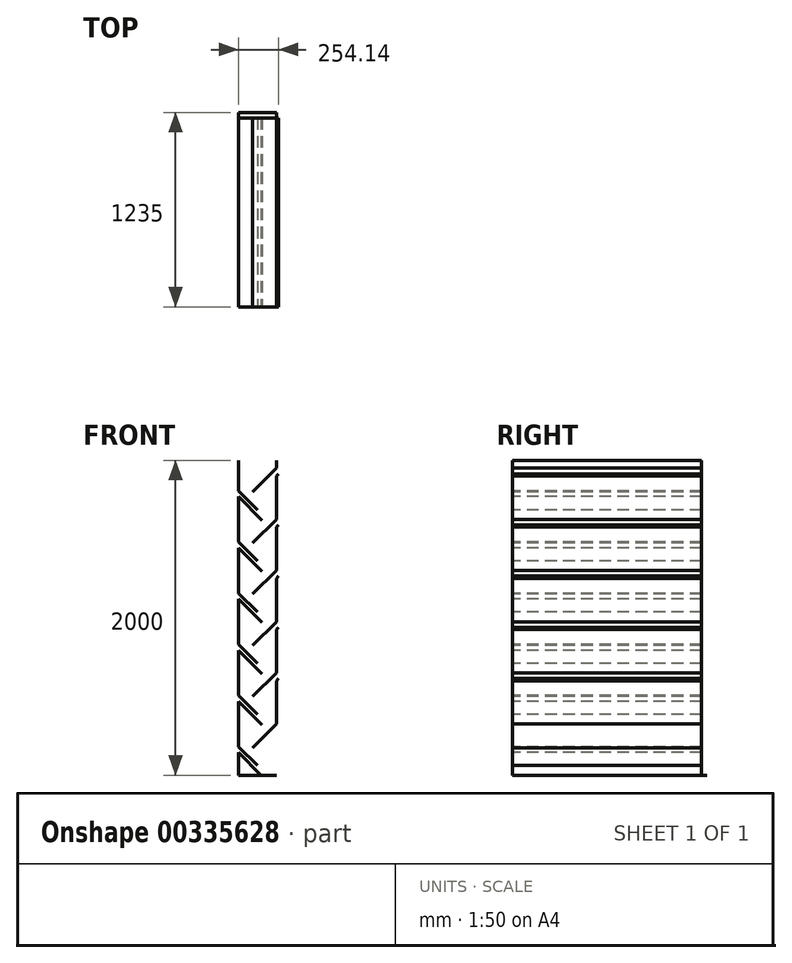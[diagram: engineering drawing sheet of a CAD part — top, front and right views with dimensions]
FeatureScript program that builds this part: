
annotation { "Feature Type Name" : "Feature", "Feature Type Description" : "" }
export const myFeature = defineFeature(function(context is Context, id is Id, definition is map)
    precondition{}
    {
        {
            var Q0;
            Q0=qCreatedBy(makeId("Front.planeOp"),FACE);
            var sketch = newSketch(context, id + "F0", { "sketchPlane" : qUnion([Q0])});
            skLineSegment(sketch, "E0", {"start": v(0, 2000) * mm, "end": v(0, 0) * mm, "construction": true});
            skLineSegment(sketch, "E1.0", {"start": v(-120, 2000) * mm, "end": v(-120, 0) * mm, "construction": true});
            skLineSegment(sketch, "E2.0", {"start": v(120, 2000) * mm, "end": v(120, 0) * mm, "construction": true});
            skLineSegment(sketch, "E3.0", {"start": v(-30, 2000) * mm, "end": v(-30, 0) * mm, "construction": true});
            skLineSegment(sketch, "E4.0", {"start": v(30, 2000) * mm, "end": v(30, 0) * mm, "construction": true});
            skLineSegment(sketch, "E5", {"start": v(-120, 2000) * mm, "end": v(120, 2000) * mm});
            skLineSegment(sketch, "E6.0", {"start": v(-120, 1950) * mm, "end": v(120, 1950) * mm, "construction": true});
            skLineSegment(sketch, "E7", {"start": v(120, 1950) * mm, "end": v(-30, 1800) * mm});
            skLineSegment(sketch, "E8", {"start": v(-120, 1805.89) * mm, "end": v(0, 1685.89) * mm});
            skLineSegment(sketch, "E9", {"start": v(-120, 1769.12) * mm, "end": v(30, 1619.12) * mm});
            skLineSegment(sketch, "E10", {"start": v(-120, 1769.12) * mm, "end": v(-120, 1480.86) * mm});
            skLineSegment(sketch, "E11", {"start": v(-120, 1480.86) * mm, "end": v(0, 1360.86) * mm});
            skLineSegment(sketch, "E12", {"start": v(-30, 1475) * mm, "end": v(120, 1625) * mm});
            skLineSegment(sketch, "E13", {"start": v(120, 1625) * mm, "end": v(120, 1900.5) * mm});
            skLineSegment(sketch, "E14", {"start": v(-120, 1805.89) * mm, "end": v(-120, 2000) * mm});
            skLineSegment(sketch, "E15", {"start": v(120, 1950) * mm, "end": v(120, 2000) * mm});
            skLineSegment(sketch, "E16", {"start": v(-120, 1444.09) * mm, "end": v(30, 1294.09) * mm});
            skLineSegment(sketch, "E17", {"start": v(-120, 1155.83) * mm, "end": v(0, 1035.83) * mm});
            skLineSegment(sketch, "E18", {"start": v(-120, 1444.09) * mm, "end": v(-120, 1155.83) * mm});
            skLineSegment(sketch, "E19", {"start": v(-30, 1149.97) * mm, "end": v(120, 1299.97) * mm});
            skLineSegment(sketch, "E20", {"start": v(120, 1299.97) * mm, "end": v(120, 1575.5) * mm});
            skLineSegment(sketch, "E21.0.1.0", {"start": v(-120, 830.76) * mm, "end": v(0, 710.76) * mm});
            skLineSegment(sketch, "E21.0.1.1", {"start": v(-120, 1119.02) * mm, "end": v(-120, 830.76) * mm});
            skLineSegment(sketch, "E21.0.1.2", {"start": v(-120, 1119.02) * mm, "end": v(30, 969.02) * mm});
            skLineSegment(sketch, "E21.0.2.0", {"start": v(-120, 505.7) * mm, "end": v(0, 385.7) * mm});
            skLineSegment(sketch, "E21.0.2.1", {"start": v(-120, 793.96) * mm, "end": v(-120, 505.7) * mm});
            skLineSegment(sketch, "E21.0.2.2", {"start": v(-120, 793.96) * mm, "end": v(30, 643.96) * mm});
            skLineSegment(sketch, "E21.direction1", {"start": v(-120, 1155.83) * mm, "end": v(-120, 1155.83) * mm});
            skLineSegment(sketch, "E21.direction2", {"start": v(-120, 1155.83) * mm, "end": v(-120, 830.76) * mm, "construction": true});
            skLineSegment(sketch, "E22.0.0.3", {"start": v(-120, 180.64) * mm, "end": v(0, 60.64) * mm});
            skLineSegment(sketch, "E22.3.0.3", {"start": v(-120, 468.9) * mm, "end": v(-120, 180.64) * mm});
            skLineSegment(sketch, "E22.6.0.3", {"start": v(-120, 468.9) * mm, "end": v(30, 318.9) * mm});
            skLineSegment(sketch, "E23.0.1.0", {"start": v(120, 974.91) * mm, "end": v(120, 1250.44) * mm});
            skLineSegment(sketch, "E23.0.1.1", {"start": v(-30, 824.91) * mm, "end": v(120, 974.91) * mm});
            skLineSegment(sketch, "E23.direction1", {"start": v(-30, 1149.97) * mm, "end": v(-30, 1149.97) * mm});
            skLineSegment(sketch, "E23.direction2", {"start": v(-30, 1149.97) * mm, "end": v(-30, 824.91) * mm, "construction": true});
            skLineSegment(sketch, "E24.0.0.2", {"start": v(120, 649.85) * mm, "end": v(120, 925.38) * mm});
            skLineSegment(sketch, "E24.3.0.2", {"start": v(-30, 499.85) * mm, "end": v(120, 649.85) * mm});
            skLineSegment(sketch, "E24.0.0.3", {"start": v(120, 324.79) * mm, "end": v(120, 600.32) * mm});
            skLineSegment(sketch, "E24.3.0.3", {"start": v(-30, 174.79) * mm, "end": v(120, 324.79) * mm});
            skLineSegment(sketch, "E25", {"start": v(-120, 143.87) * mm, "end": v(23.87, 0) * mm});
            skLineSegment(sketch, "E26", {"start": v(-120, 0) * mm, "end": v(120, 0) * mm});
            skLineSegment(sketch, "E27", {"start": v(120, 0) * mm, "end": v(120, 275.3) * mm});
            skLineSegment(sketch, "E28", {"start": v(120, 1900.5) * mm, "end": v(134.14, 1914.64) * mm});
            skLineSegment(sketch, "E29", {"start": v(-120, 0) * mm, "end": v(-120, 143.87) * mm});
            skLineSegment(sketch, "E30", {"start": v(120, 1575.5) * mm, "end": v(134.14, 1589.65) * mm});
            skLineSegment(sketch, "E31.0.1.0", {"start": v(120, 1250.44) * mm, "end": v(134.14, 1264.58) * mm});
            skLineSegment(sketch, "E31.0.2.0", {"start": v(120, 925.38) * mm, "end": v(134.14, 939.52) * mm});
            skLineSegment(sketch, "E31.0.3.0", {"start": v(120, 600.32) * mm, "end": v(134.14, 614.46) * mm});
            skLineSegment(sketch, "E31.direction1", {"start": v(120, 1575.5) * mm, "end": v(145, 1575.5) * mm, "construction": true});
            skLineSegment(sketch, "E31.direction2", {"start": v(120, 1575.5) * mm, "end": v(120, 1250.44) * mm, "construction": true});
            skLineSegment(sketch, "E32.0.0.4", {"start": v(120, 275.26) * mm, "end": v(134.14, 289.4) * mm});
            skSolve(sketch);
        }
        {
            var Q0;
            Q0 = qSketchRegion(id + "F0", true);
            var Q1;
            Q1=sQuery(id+"F0.wireOp",EDGE,"E25");
            var Q2;
            Q2=sQuery(id+"F0.wireOp",EDGE,"E29");
            var Q3;
            Q3=sQuery(id+"F0.wireOp",EDGE,"E22.0.0.3");
            var Q4;
            Q4=sQuery(id+"F0.wireOp",EDGE,"E22.6.0.3");
            var Q5;
            Q5=sQuery(id+"F0.wireOp",EDGE,"E21.0.2.0");
            var Q6;
            Q6=sQuery(id+"F0.wireOp",EDGE,"E21.0.2.1");
            var Q7;
            Q7=sQuery(id+"F0.wireOp",EDGE,"E21.0.2.2");
            var Q8;
            Q8=sQuery(id+"F0.wireOp",EDGE,"E22.3.0.3");
            var Q9;
            Q9=sQuery(id+"F0.wireOp",EDGE,"E24.0.0.3");
            var Q10;
            Q10=sQuery(id+"F0.wireOp",EDGE,"E31.0.3.0");
            var Q11;
            Q11=sQuery(id+"F0.wireOp",EDGE,"E24.3.0.2");
            var Q12;
            Q12=sQuery(id+"F0.wireOp",EDGE,"E24.0.0.2");
            var Q13;
            Q13=sQuery(id+"F0.wireOp",EDGE,"E31.0.2.0");
            var Q14;
            Q14=sQuery(id+"F0.wireOp",EDGE,"E23.0.1.1");
            var Q15;
            Q15=sQuery(id+"F0.wireOp",EDGE,"E21.0.1.0");
            var Q16;
            Q16=sQuery(id+"F0.wireOp",EDGE,"E21.0.1.2");
            var Q17;
            Q17=sQuery(id+"F0.wireOp",EDGE,"E21.0.1.1");
            var Q18;
            Q18=sQuery(id+"F0.wireOp",EDGE,"E17");
            var Q19;
            Q19=sQuery(id+"F0.wireOp",EDGE,"E23.0.1.0");
            var Q20;
            Q20=sQuery(id+"F0.wireOp",EDGE,"E18");
            var Q21;
            Q21=sQuery(id+"F0.wireOp",EDGE,"E19");
            var Q22;
            Q22=sQuery(id+"F0.wireOp",EDGE,"E31.0.1.0");
            var Q23;
            Q23=sQuery(id+"F0.wireOp",EDGE,"E20");
            var Q24;
            Q24=sQuery(id+"F0.wireOp",EDGE,"E16");
            var Q25;
            Q25=sQuery(id+"F0.wireOp",EDGE,"E11");
            var Q26;
            Q26=sQuery(id+"F0.wireOp",EDGE,"E12");
            var Q27;
            Q27=sQuery(id+"F0.wireOp",EDGE,"E10");
            var Q28;
            Q28=sQuery(id+"F0.wireOp",EDGE,"E9");
            var Q29;
            Q29=sQuery(id+"F0.wireOp",EDGE,"E30");
            var Q30;
            Q30=sQuery(id+"F0.wireOp",EDGE,"E8");
            var Q31;
            Q31=sQuery(id+"F0.wireOp",EDGE,"E14");
            var Q32;
            Q32=sQuery(id+"F0.wireOp",EDGE,"E13");
            var Q33;
            Q33=sQuery(id+"F0.wireOp",EDGE,"E28");
            var Q34;
            Q34=sQuery(id+"F0.wireOp",EDGE,"E7");
            var Q35;
            Q35=sQuery(id+"F0.wireOp",EDGE,"E15");
            var Q36;
            Q36=sQuery(id+"F0.wireOp",EDGE,"E24.3.0.3");
            extrude(context, id + "F1", {"entities" : qUnion([Q0]), "bodyType" : ToolBodyType.SURFACE, "surfaceEntities" : qUnion([Q1, Q2, Q3, Q4, Q5, Q6, Q7, Q8, Q9, Q10, Q11, Q12, Q13, Q14, Q15, Q16, Q17, Q18, Q19, Q20, Q21, Q22, Q23, Q24, Q25, Q26, Q27, Q28, Q29, Q30, Q31, Q32, Q33, Q34, Q35, Q36]), "depth" : 1200 * mm, "offsetDistance" : 25 * mm});
        }
        {
            var Q0;
            Q0=sQuery(id+"F0.wireOp",EDGE,"E26");
            extrude(context, id + "F2", {"bodyType" : ToolBodyType.SURFACE, "surfaceEntities" : qUnion([Q0]), "oppositeDirection" : true, "depth" : 35 * mm, "offsetDistance" : 25 * mm});
        }
    });
